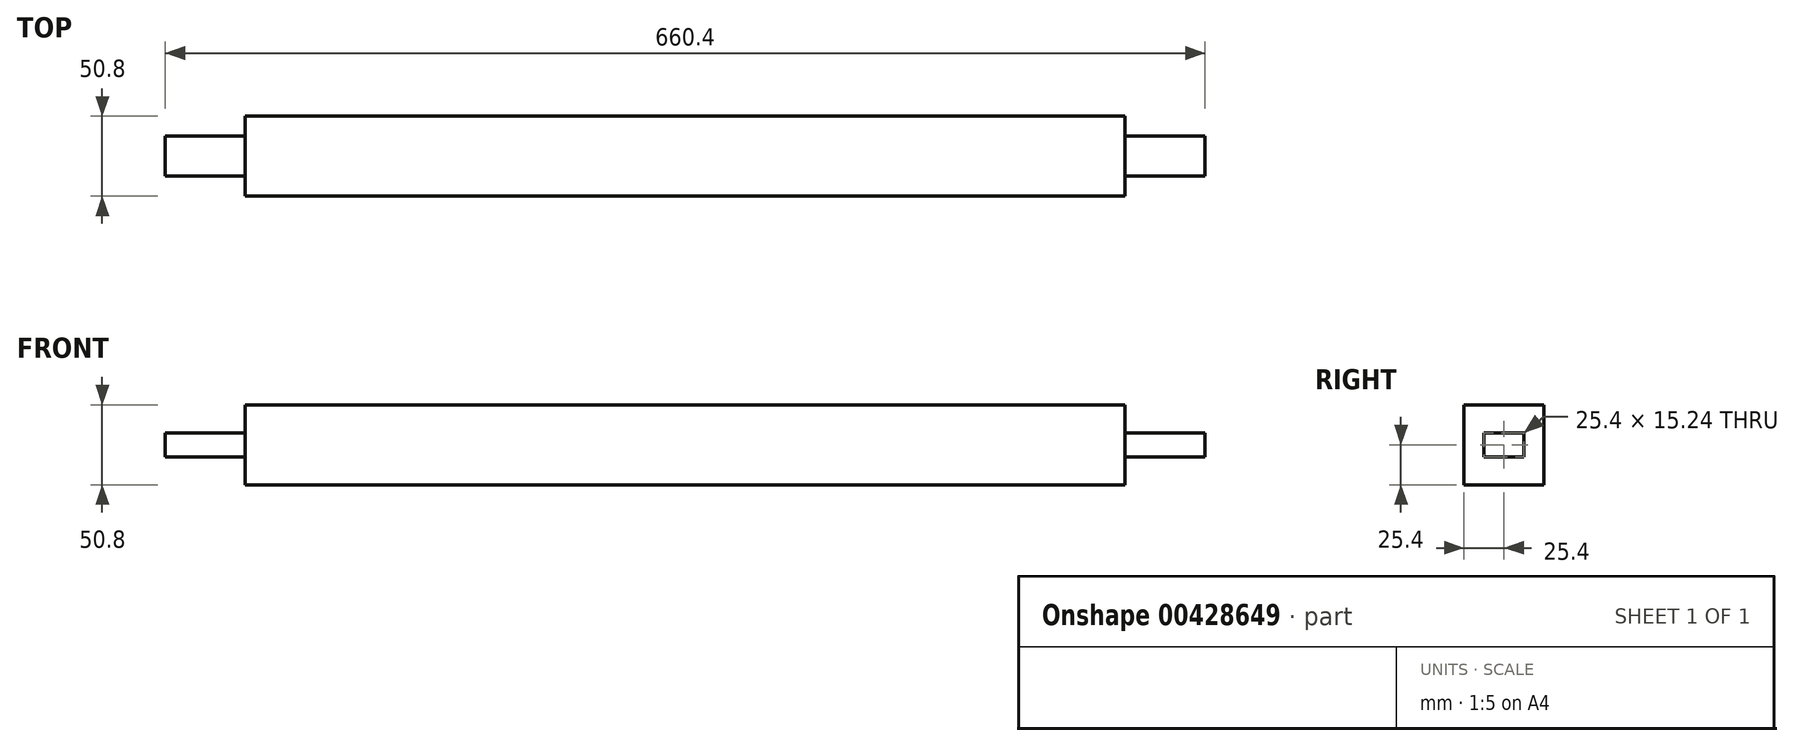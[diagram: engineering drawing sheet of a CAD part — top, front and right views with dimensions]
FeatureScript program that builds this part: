
annotation { "Feature Type Name" : "Feature", "Feature Type Description" : "" }
export const myFeature = defineFeature(function(context is Context, id is Id, definition is map)
    precondition{}
    {
        {
            var Q0;
            Q0=qCreatedBy(makeId("Top.planeOp"),FACE);
            var sketch = newSketch(context, id + "F0", { "sketchPlane" : qUnion([Q0])});
            skLineSegment(sketch, "E0.bottom", {"start": v(-330.2, 25.4) * mm, "end": v(330.2, 25.4) * mm});
            skLineSegment(sketch, "E0.top", {"start": v(-330.2, -25.4) * mm, "end": v(330.2, -25.4) * mm});
            skLineSegment(sketch, "E0.left", {"start": v(-330.2, 25.4) * mm, "end": v(-330.2, -25.4) * mm});
            skLineSegment(sketch, "E0.right", {"start": v(330.2, 25.4) * mm, "end": v(330.2, -25.4) * mm});
            skPoint(sketch, "E0.middle", {"position": v(0, 0) * mm});
            skSolve(sketch);
        }
        {
            var Q0;
            Q0=makeQuery(id+"F0.imprint","IMPRINT",FACE,{"disambiguationData":[TD([[makeQuery(id+"F0.imprint","IMPRINT",EDGE,{"derivedFrom":sQuery(id+"F0.wireOp",EDGE,"E0.bottom")}),-1.0]])]});
            extrude(context, id + "F1", {"entities" : qUnion([Q0]), "depth" : 50.8 * mm});
        }
        {
            var Q0;
            Q0=makeQuery(id+"F1.opExtrude","SWEPT_FACE",FACE,{"disambiguationData":[OSD([sQuery(id+"F0.wireOp",EDGE,"E0.left")])]});
            var sketch = newSketch(context, id + "F2", { "sketchPlane" : qUnion([Q0])});
            skPoint(sketch, "E1.endSnap0", {"position": v(0, 50.8) * mm});
            skLineSegment(sketch, "E2.bottom", {"start": v(-12.7, 33.02) * mm, "end": v(12.7, 33.02) * mm});
            skLineSegment(sketch, "E2.top", {"start": v(-12.7, 17.78) * mm, "end": v(12.7, 17.78) * mm});
            skLineSegment(sketch, "E2.left", {"start": v(-12.7, 33.02) * mm, "end": v(-12.7, 17.78) * mm});
            skLineSegment(sketch, "E2.right", {"start": v(12.7, 33.02) * mm, "end": v(12.7, 17.78) * mm});
            skPoint(sketch, "E2.middle", {"position": v(0, 25.4) * mm});
            skPoint(sketch, "E2.cornerSnap0", {"position": v(-3.9, 33.02) * mm});
            skLineSegment(sketch, "E3.bottom", {"start": v(-25.4, 50.8) * mm, "end": v(25.4, 50.8) * mm});
            skLineSegment(sketch, "E3.top", {"start": v(-25.4, 0) * mm, "end": v(25.4, 0) * mm});
            skLineSegment(sketch, "E3.left", {"start": v(-25.4, 50.8) * mm, "end": v(-25.4, 0) * mm});
            skLineSegment(sketch, "E3.right", {"start": v(25.4, 50.8) * mm, "end": v(25.4, 0) * mm});
            skSolve(sketch);
        }
        {
            var Q0;
            Q0 = qSketchRegion(id + "F2", true);
            extrude(context, id + "F3", {"entities" : qUnion([Q0]), "operationType" : NewBodyOperationType.REMOVE, "oppositeDirection" : true, "depth" : 50.8 * mm});
        }
        {
            var Q0;
            Q0=makeQuery(id+"F1.opExtrude","SWEPT_FACE",FACE,{"disambiguationData":[OSD([sQuery(id+"F0.wireOp",EDGE,"E0.right")])]});
            var sketch = newSketch(context, id + "F4", { "sketchPlane" : qUnion([Q0])});
            skLineSegment(sketch, "E4", {"start": v(-25.4, 17.78) * mm, "end": v(-25.4, 0) * mm});
            skLineSegment(sketch, "E5", {"start": v(-25.4, 0) * mm, "end": v(0, 0) * mm});
            skLineSegment(sketch, "E6", {"start": v(25.4, 17.78) * mm, "end": v(25.4, 0) * mm});
            skLineSegment(sketch, "E7", {"start": v(25.4, 0) * mm, "end": v(0, 0) * mm});
            skPoint(sketch, "E8.endSnap0", {"position": v(0, 50.8) * mm});
            skLineSegment(sketch, "E9", {"start": v(-25.4, 33.02) * mm, "end": v(-25.4, 50.8) * mm});
            skLineSegment(sketch, "E10", {"start": v(-25.4, 50.8) * mm, "end": v(0, 50.8) * mm});
            skLineSegment(sketch, "E11", {"start": v(25.4, 50.8) * mm, "end": v(25.4, 33.02) * mm});
            skLineSegment(sketch, "E12", {"start": v(0, 50.8) * mm, "end": v(25.4, 50.8) * mm});
            skLineSegment(sketch, "E13", {"start": v(0, 50.8) * mm, "end": v(-25.4, 50.8) * mm});
            skLineSegment(sketch, "E14", {"start": v(-12.7, 25.4) * mm, "end": v(-12.7, 33.02) * mm});
            skLineSegment(sketch, "E15", {"start": v(-12.7, 33.02) * mm, "end": v(-12.7, 17.78) * mm});
            skLineSegment(sketch, "E16", {"start": v(12.7, 25.4) * mm, "end": v(12.7, 33.02) * mm});
            skLineSegment(sketch, "E17", {"start": v(12.7, 25.4) * mm, "end": v(12.7, 17.78) * mm});
            skLineSegment(sketch, "E18", {"start": v(-25.4, 50.8) * mm, "end": v(-25.4, 0) * mm});
            skLineSegment(sketch, "E19", {"start": v(-25.4, 0) * mm, "end": v(25.4, 0) * mm});
            skLineSegment(sketch, "E20", {"start": v(25.4, 0) * mm, "end": v(25.4, 50.8) * mm});
            skLineSegment(sketch, "E21", {"start": v(25.4, 50.8) * mm, "end": v(-25.4, 50.8) * mm});
            skLineSegment(sketch, "E22", {"start": v(-25.4, 33.02) * mm, "end": v(-12.7, 33.02) * mm});
            skLineSegment(sketch, "E23", {"start": v(-12.7, 17.78) * mm, "end": v(-25.4, 17.78) * mm});
            skLineSegment(sketch, "E24", {"start": v(12.7, 33.02) * mm, "end": v(25.4, 33.02) * mm});
            skLineSegment(sketch, "E25", {"start": v(12.7, 17.78) * mm, "end": v(25.4, 17.78) * mm});
            skLineSegment(sketch, "E26", {"start": v(12.7, 33.02) * mm, "end": v(-12.7, 33.02) * mm});
            skLineSegment(sketch, "E27", {"start": v(-12.7, 17.78) * mm, "end": v(12.7, 17.78) * mm});
            skLineSegment(sketch, "E28", {"start": v(25.4, 33.02) * mm, "end": v(25.4, 17.78) * mm});
            skLineSegment(sketch, "E29", {"start": v(-25.4, 33.02) * mm, "end": v(-25.4, 17.78) * mm});
            skSolve(sketch);
        }
        {
            var Q0;
            Q0 = qSketchRegion(id + "F4", true);
            extrude(context, id + "F5", {"entities" : qUnion([Q0]), "operationType" : NewBodyOperationType.REMOVE, "oppositeDirection" : true, "depth" : 50.8 * mm});
        }
    });
